# Revit family: BOS-Oberlicht-Seitenteilzarge-TUud-STW_Familie
name_source: partatom
category: Türen
revit_build: Autodesk Revit 2017 (Build: 20160225_1515(x64)
units: mm (PartAtom-declared; Revit-internal decimal feet)

## family parameters
Basisbauteil = Wand
Beim Laden mit Abzugskörper schneiden = Nein
Gemeinsam genutzt = Nein
Immer vertikal = Ja
Raumberechnungspunkt = Ja

## types (3) — shared parameters
Aluminiumglasleistenbreite = 12 mm  [stored 0.0393701 ft]
Aluminiumglasleistenhöhe = 15 mm  [stored 0.0492126 ft]
BBL1 Bandbezugslinie   Hinge Position 1 = 241 mm  [stored 0.790682 ft]
BE max. = 100 mm  [stored 0.328084 ft]
Bauelement = BOS Stahlzarge
Blechstärke = 1.5 mm  [stored 0.00492126 ft]
Doppelfalz = Nein
Drehpunkt Warnung sichtbar = Ja
Drehpunktreferenz horizontal = 500 mm  [stored 1.64042 ft]
Einfachfalz = Ja
FMB Seitenteil max. = 1000 mm  [stored 3.28084 ft]
FMB Seitenteil min. = 100 mm  [stored 0.328084 ft]
FMB Türblatt max. = 1341 mm  [stored 4.39961 ft]
FMB Türblatt min. = 591 mm  [stored 1.93898 ft]
FMH Oberlicht max. = 1000 mm  [stored 3.28084 ft]
FMH Oberlicht min. = 100 mm  [stored 0.328084 ft]
FMH Türblatt max. = 2483 mm
FMH Türblatt min. = 1608 mm
Falzaufschlag = 15 mm  [stored 0.0492126 ft]
Falzaufschlag gesamt = 15 mm  [stored 0.0492126 ft]
Falztiefe 2 = 23 mm  [stored 0.0754593 ft]
Funktion = Innen
GT max. = 650 mm  [stored 2.13255 ft]
Hersteller = BOS GmbH Best Of Steel, Lütkenfelde 4, D-48282 Emsdetten
Info-Texte sichtbar = Ja
Information in English = Nein
Leibungstiefe Kämpfer max. = 23 mm  [stored 0.0754593 ft]
Leibungstiefe Kämpfer min. = 23 mm  [stored 0.0754593 ft]
Material = grundiert, feuerverzinktes Feinblech nach DIN EN 10143
Material - Acrylfuge = <Nach Kategorie>
Material - Bänder = <Nach Kategorie>
Material - Dichtung = <Nach Kategorie>
Material - Drückergarnitur = <Nach Kategorie>
Material - Eckabdeckung = <Nach Kategorie>
Material - Glasleisten = <Nach Kategorie>
Material - Türblatt = <Nach Kategorie>
Material - Verglasung = Glas
Material - Vorlegeband = <Nach Kategorie>
Material - Zarge = <Nach Kategorie>
Profilverschiebung = 30 mm  [stored 0.0984252 ft]
Putzwinkel max. = 28 mm  [stored 0.0918635 ft]
Putzwinkel min. = 10 mm  [stored 0.0328084 ft]
Rohrglasleistenbreite = 10 mm  [stored 0.0328084 ft]
Rohrglasleistenhöhe = 15 mm  [stored 0.0492126 ft]
Rohrglasleistenprofilverschiebung horizontal = 7.5 mm  [stored 0.0246063 ft]
Rohrglasleistenprofilverschiebung vertikal = -5 mm  [stored -0.0164042 ft]
Sickentiefe = 10 mm  [stored 0.0328084 ft]
Spiegel innen max. = 45 mm  [stored 0.147638 ft]
Spiegel vorne max. = 80 mm  [stored 0.262467 ft]
Spiegel vorne min. = 30 mm  [stored 0.0984252 ft]
Technische Infos rund um die Stahlzarge = www.BestOfSteel.de/tools-downloads/technische-infos-rund-um-die-stahlzarge/
Türblattabstand 2 = 4.5 mm  [stored 0.0147638 ft]
Türblattabstand 3 = 4.5 mm  [stored 0.0147638 ft]
Türblattabstand links-rechts = 3.5 mm  [stored 0.0114829 ft]
Türblattabstand oben = 4 mm  [stored 0.0131234 ft]
Türblattabstand unten = 7 mm  [stored 0.0229659 ft]
Türblattaufschlag = 13 mm
Türblattstärke = 65 mm  [stored 0.213255 ft]
Türblattstärke 3 = 25 mm  [stored 0.082021 ft]
URL = www.BestOfSteel.de/stahlzargen/zargen-fuer-drehfluegeltueren/elementzargen/oberlicht-seitenteilzargen/
Öffnungswinkel min. = 0.00°
zero-valued in all types: Breite, Dicke, Rohbaubreite, Rohbauhöhe

## per-type parameters (varying)
| type | Beschreibung | Drehpunktabstand (FM) horizontal | Drehpunktabstand (SP) vertikal | Falztiefe | Falztiefe gesamt | Gefälzt | Modell | Stumpf | TUsd/KEsd (Bandrolle sichtbar) | TUsd/KEsd (verdeckt liegendes Band) | TUud/KEud | Türblattabstand 1 | Türblattstärke 1 | Türblattstärke 2 | Türblattversatz  horizontal | Türblattversatz vertikal |
| TUud/KEud | Oberlicht-/Seitenteilzarge als Leibungsprofil Planar Variante 1 für Ständerwerk, gefälzt | 21 mm  [stored 0.0688976 ft] | 12.5 mm  [stored 0.0410105 ft] | 28.5 mm  [stored 0.0935039 ft] | 28.5 mm  [stored 0.0935039 ft] | Ja | TUud/KEud | Nein | Nein | Nein | Ja | 1.5 mm  [stored 0.00492126 ft] | 14.5 mm  [stored 0.0475722 ft] | 25.5 mm  [stored 0.0836614 ft] | 11.5 mm  [stored 0.0377297 ft] | -3.5 mm  [stored -0.0114829 ft] |
| TUsd/KEsd (Bandrolle sichtbar) | Oberlicht-/Seitenteilzarge als Leibungsprofil Planar Variante 1 für Ständerwerk, stumpf (Bandrolle sichtbar) | 2.5 mm  [stored 0.0082021 ft] | 13.5 mm  [stored 0.0442913 ft] | 46.5 mm  [stored 0.152559 ft] | 46.5 mm  [stored 0.152559 ft] | Nein | TUsd/KEsd | Ja | Ja | Nein | Nein | -2 mm  [stored -0.00656168 ft] | 0 mm  [stored 0 ft] | 40 mm  [stored 0.131234 ft] | 6 mm  [stored 0.019685 ft] | 15.5 mm  [stored 0.050853 ft] |
| TUsd/KEsd (verdeckt liegendes Band) | Oberlicht-/Seitenteilzarge als Leibungsprofil Planar Variante 1 für Ständerwerk, stumpf (verdeckt liegendes Band) | 2.5 mm  [stored 0.0082021 ft] | 13.5 mm  [stored 0.0442913 ft] | 46.5 mm  [stored 0.152559 ft] | 46.5 mm  [stored 0.152559 ft] | Nein | TUsd/KEsd | Ja | Nein | Ja | Nein | -2 mm  [stored -0.00656168 ft] | 0 mm  [stored 0 ft] | 40 mm  [stored 0.131234 ft] | 6 mm  [stored 0.019685 ft] | 15.5 mm  [stored 0.050853 ft] |

note: [stored X ft] marks values corroborated as IEEE doubles in the binary element streams (Revit-internal decimal feet)
